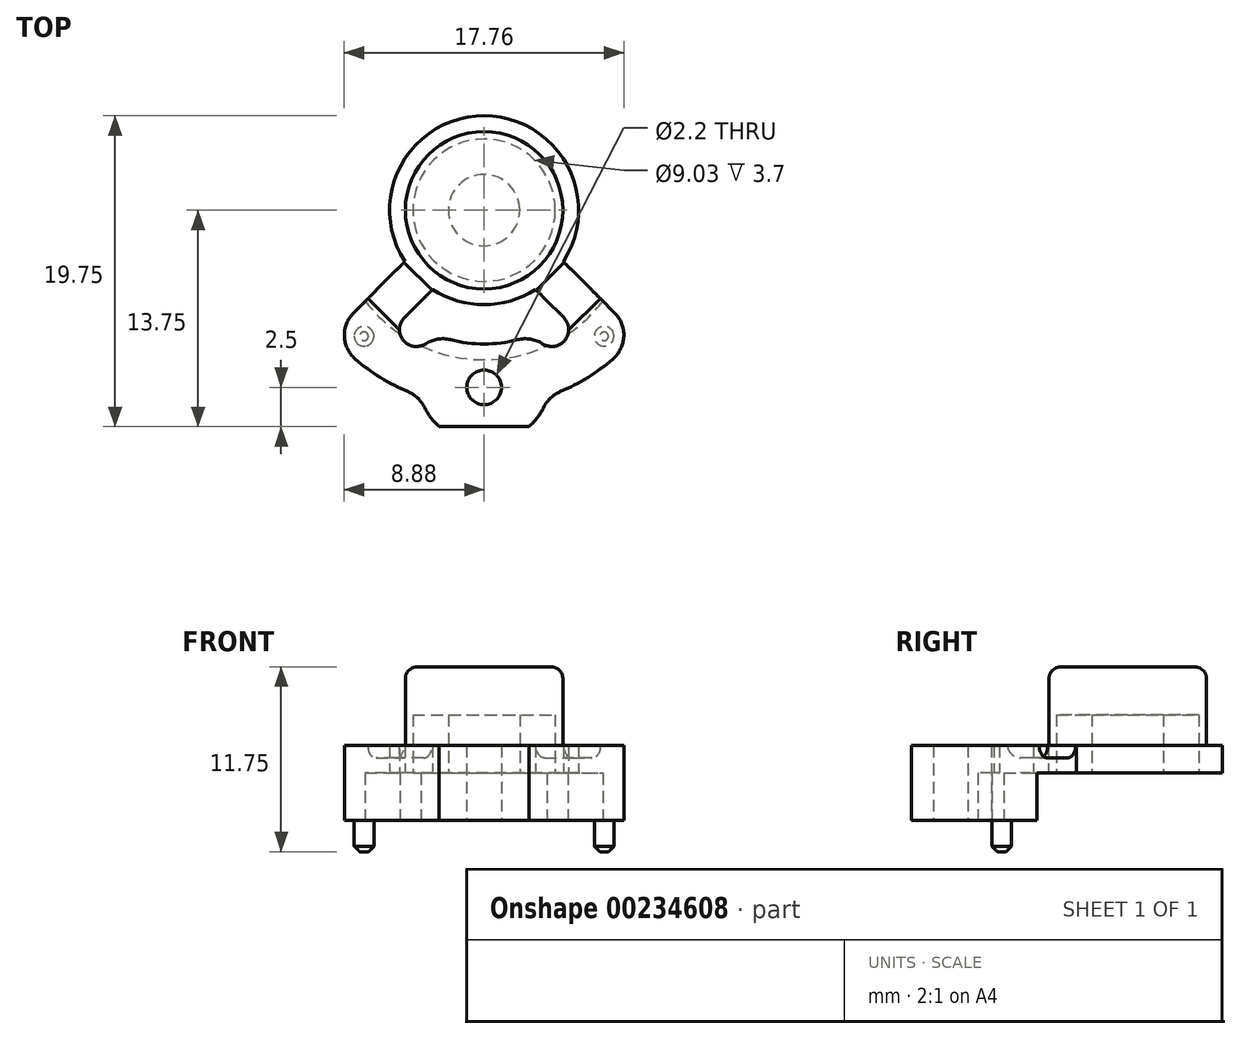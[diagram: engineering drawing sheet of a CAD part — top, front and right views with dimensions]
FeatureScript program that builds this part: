
annotation { "Feature Type Name" : "Feature", "Feature Type Description" : "" }
export const myFeature = defineFeature(function(context is Context, id is Id, definition is map)
    precondition{}
    {
        {
            var Q0;
            Q0=qCreatedBy(makeId("Top.planeOp"),FACE);
            var sketch = newSketch(context, id + "F0", { "sketchPlane" : qUnion([Q0])});
            skLineSegment(sketch, "E0.bottom", {"start": v(4, 3) * mm, "end": v(-4, 3) * mm, "construction": true});
            skLineSegment(sketch, "E0.top", {"start": v(4, -3) * mm, "end": v(-4, -3) * mm, "construction": true});
            skLineSegment(sketch, "E0.left", {"start": v(4, 3) * mm, "end": v(4, -3) * mm, "construction": true});
            skLineSegment(sketch, "E0.right", {"start": v(-4, 3) * mm, "end": v(-4, -3) * mm, "construction": true});
            skPoint(sketch, "E0.middle", {"position": v(0, 0) * mm});
            skArc(sketch, "E1", {"start": v(-9.68, -7.91) * mm, "mid": v(-7.15, -10.25) * mm, "end": v(-4.08, -11.82) * mm});
            skArc(sketch, "E2.converted", {"start": v(-3.27, -5.03) * mm, "mid": v(0, -6) * mm, "end": v(3.27, -5.03) * mm});
            skPoint(sketch, "E3.orphan", {"position": v(-6, 0) * mm});
            skLineSegment(sketch, "E4", {"start": v(0, 0) * mm, "end": v(14.62, -14.62) * mm, "construction": true});
            skLineSegment(sketch, "E5", {"start": v(5.03, -3.27) * mm, "end": v(9.68, -7.91) * mm});
            skLineSegment(sketch, "E6.MirrorCS", {"start": v(3.27, -5.03) * mm, "end": v(5.06, -6.83) * mm});
            skLineSegment(sketch, "E7.MirrorCS", {"start": v(-5.03, -3.27) * mm, "end": v(-9.68, -7.91) * mm});
            skLineSegment(sketch, "E8.MirrorCS", {"start": v(-3.27, -5.03) * mm, "end": v(-5.06, -6.83) * mm});
            skArc(sketch, "E9.MirrorCS", {"start": v(5.06, -6.83) * mm, "mid": v(4.83, -8.52) * mm, "end": v(3.27, -7.85) * mm});
            skArc(sketch, "E10.MirrorCS", {"start": v(-5.06, -6.83) * mm, "mid": v(-4.83, -8.52) * mm, "end": v(-3.27, -7.85) * mm});
            skArc(sketch, "E11.trimOffspring", {"start": v(-3.27, -7.85) * mm, "mid": v(0, -8.5) * mm, "end": v(3.27, -7.85) * mm});
            skArc(sketch, "E12.trimOffspring", {"start": v(5.03, -3.27) * mm, "mid": v(0, 6) * mm, "end": v(-5.03, -3.27) * mm});
            skArc(sketch, "E13.trimOffspring", {"start": v(4.08, -11.82) * mm, "mid": v(7.15, -10.25) * mm, "end": v(9.68, -7.91) * mm});
            skArc(sketch, "E14.trimOffspring", {"start": v(-4.08, -11.82) * mm, "mid": v(-3.6, -12.87) * mm, "end": v(-2.85, -13.75) * mm});
            skCircle(sketch, "E15", {"center": v(0, -11.25) * mm, "radius": 1.1 * mm});
            skPoint(sketch, "E16.orphan", {"position": v(-13.8, -3.13) * mm});
            skPoint(sketch, "E17.orphan", {"position": v(12.5, 0) * mm});
            skPoint(sketch, "E18.orphan", {"position": v(13.8, -3.13) * mm});
            skLineSegment(sketch, "E19", {"start": v(-2.85, -13.75) * mm, "end": v(2.85, -13.75) * mm});
            skArc(sketch, "E20.trimOffspring", {"start": v(2.85, -13.75) * mm, "mid": v(3.6, -12.87) * mm, "end": v(4.08, -11.82) * mm});
            skPoint(sketch, "E21.orphan", {"position": v(-6.83, -5.06) * mm});
            skPoint(sketch, "E22.start.orphan", {"position": v(-8.34, -1.67) * mm});
            skPoint(sketch, "E23.MirrorCS.end.orphan", {"position": v(-7.85, -3.27) * mm});
            skPoint(sketch, "E24.trimOffspring.end.orphan", {"position": v(8.34, -1.67) * mm});
            skPoint(sketch, "E25.end.orphan", {"position": v(7.85, -3.27) * mm});
            skPoint(sketch, "E25.start.orphan", {"position": v(6.83, -5.06) * mm});
            skSolve(sketch);
        }
        {
            var Q0;
            Q0=qSketchRegion(id+"F0",true);
            extrude(context, id + "F1", {"entities" : qUnion([Q0]), "depth" : 4.75 * mm});
        }
        {
            var Q0;
            Q0=makeQuery(id+"F1.opExtrude","CAP_FACE",FACE,{"disambiguationData":[OSD([sQuery(id+"F0.wireOp",EDGE,"E1"),sQuery(id+"F0.wireOp",EDGE,"E2.converted"),sQuery(id+"F0.wireOp",EDGE,"rdbc6vYB-NVjA-jXWY-TLaR-nZ7SSUkQD9Vy"),sQuery(id+"F0.wireOp",EDGE,"ynKpnGIP-DJsh-uGPF-F4s2-QlGlmaUKXdbb"),sQuery(id+"F0.wireOp",EDGE,"E22"),sQuery(id+"F0.wireOp",EDGE,"E5"),sQuery(id+"F0.wireOp",EDGE,"E6.MirrorCS"),sQuery(id+"F0.wireOp",EDGE,"E7.MirrorCS"),sQuery(id+"F0.wireOp",EDGE,"E8.MirrorCS"),sQuery(id+"F0.wireOp",EDGE,"E25"),sQuery(id+"F0.wireOp",EDGE,"E9.MirrorCS"),sQuery(id+"F0.wireOp",EDGE,"E24.trimOffspring"),sQuery(id+"F0.wireOp",EDGE,"E10.MirrorCS"),sQuery(id+"F0.wireOp",EDGE,"E23.MirrorCS"),sQuery(id+"F0.wireOp",EDGE,"E11.trimOffspring"),sQuery(id+"F0.wireOp",EDGE,"E12.trimOffspring")])],"isStart":false});
            var sketch = newSketch(context, id + "F2", { "sketchPlane" : qUnion([Q0])});
            skCircle(sketch, "E26", {"center": v(0, 0) * mm, "radius": 5 * mm});
            skSolve(sketch);
        }
        {
            var Q0;
            Q0=makeQuery(id+"F2.imprint","IMPRINT",FACE,{"disambiguationData":[TD([[makeQuery(id+"F2.imprint","IMPRINT",EDGE,{"derivedFrom":sQuery(id+"F2.wireOp",EDGE,"E26")}),1.0]])]});
            extrude(context, id + "F3", {"entities" : qUnion([Q0]), "operationType" : NewBodyOperationType.ADD, "depth" : 5 * mm});
        }
        {
            var Q0;
            Q0=makeQuery(id+"F1.opExtrude","CAP_FACE",FACE,{"disambiguationData":[OSD([sQuery(id+"F0.wireOp",EDGE,"E1"),sQuery(id+"F0.wireOp",EDGE,"E2.converted"),sQuery(id+"F0.wireOp",EDGE,"rdbc6vYB-NVjA-jXWY-TLaR-nZ7SSUkQD9Vy"),sQuery(id+"F0.wireOp",EDGE,"ynKpnGIP-DJsh-uGPF-F4s2-QlGlmaUKXdbb"),sQuery(id+"F0.wireOp",EDGE,"E22"),sQuery(id+"F0.wireOp",EDGE,"E5"),sQuery(id+"F0.wireOp",EDGE,"E6.MirrorCS"),sQuery(id+"F0.wireOp",EDGE,"E7.MirrorCS"),sQuery(id+"F0.wireOp",EDGE,"E8.MirrorCS"),sQuery(id+"F0.wireOp",EDGE,"E25"),sQuery(id+"F0.wireOp",EDGE,"E9.MirrorCS"),sQuery(id+"F0.wireOp",EDGE,"E24.trimOffspring"),sQuery(id+"F0.wireOp",EDGE,"E10.MirrorCS"),sQuery(id+"F0.wireOp",EDGE,"E23.MirrorCS"),sQuery(id+"F0.wireOp",EDGE,"E11.trimOffspring"),sQuery(id+"F0.wireOp",EDGE,"E12.trimOffspring")])],"isStart":false});
            var sketch = newSketch(context, id + "F4", { "sketchPlane" : qUnion([Q0])});
            skSolve(sketch);
        }
        {
            var Q0;
            Q0=makeQuery(id+"F1.opExtrude","SWEPT_EDGE",EDGE,{"disambiguationData":[OSD([sQuery(id+"F0.wireOp",EDGE,"E13.trimOffspring"),sQuery(id+"F0.wireOp",EDGE,"4655be30-1c85-40b4-9377-04363eb3a74c0.MirrorCS")])]});
            var Q1;
            Q1=makeQuery(id+"F1.opExtrude","SWEPT_EDGE",EDGE,{"disambiguationData":[OSD([sQuery(id+"F0.wireOp",EDGE,"E24.trimOffspring"),sQuery(id+"F0.wireOp",EDGE,"4655be30-1c85-40b4-9377-04363eb3a74c0.MirrorCS")])]});
            var Q2;
            Q2=makeQuery(id+"F1.opExtrude","SWEPT_EDGE",EDGE,{"disambiguationData":[OSD([sQuery(id+"F0.wireOp",EDGE,"E22"),sQuery(id+"F0.wireOp",EDGE,"H8J9w45X-FC2Y-JR27-rPcr-O6LJdDO2wVvT")])]});
            var Q3;
            Q3=makeQuery(id+"F1.opExtrude","SWEPT_EDGE",EDGE,{"disambiguationData":[OSD([sQuery(id+"F0.wireOp",EDGE,"E1"),sQuery(id+"F0.wireOp",EDGE,"H8J9w45X-FC2Y-JR27-rPcr-O6LJdDO2wVvT")])]});
            var Q4;
            Q4=makeQuery(id+"F1.opExtrude","SWEPT_EDGE",EDGE,{"disambiguationData":[OSD([sQuery(id+"F0.wireOp",EDGE,"E9.MirrorCS"),sQuery(id+"F0.wireOp",EDGE,"E11.trimOffspring")])]});
            var Q5;
            Q5=makeQuery(id+"F1.opExtrude","SWEPT_EDGE",EDGE,{"disambiguationData":[OSD([sQuery(id+"F0.wireOp",EDGE,"E10.MirrorCS"),sQuery(id+"F0.wireOp",EDGE,"E11.trimOffspring")])]});
            fillet(context, id + "F5", {"entities" : qUnion([Q0, Q1, Q2, Q3, Q4, Q5]), "radius" : 2 * mm, "tangentPropagation" : true, "allowEdgeOverflow" : false});
        }
        {
            var Q0;
            Q0=makeQuery(id+"F4.imprint","IMPRINT",FACE,{"disambiguationData":[TD([[makeQuery(id+"F4.imprint","IMPRINT",EDGE,{"derivedFrom":makeQuery(id+"F1.opExtrude","CAP_EDGE",EDGE,{"disambiguationData":[OSD([sQuery(id+"F0.wireOp",EDGE,"E1")])],"isStart":false})}),1.0]])]});
            var sketch = newSketch(context, id + "F6", { "sketchPlane" : qUnion([Q0])});
            skLineSegment(sketch, "E27", {"start": v(0, 0) * mm, "end": v(16.52, -16.52) * mm, "construction": true});
            skLineSegment(sketch, "E28", {"start": v(8.62, -4.38) * mm, "end": v(4.38, -8.62) * mm});
            skLineSegment(sketch, "E29", {"start": v(4.38, -8.62) * mm, "end": v(2.08, -6.32) * mm});
            skLineSegment(sketch, "E30", {"start": v(2.08, -6.32) * mm, "end": v(6.3, -2.1) * mm});
            skLineSegment(sketch, "E31", {"start": v(6.3, -2.1) * mm, "end": v(8.62, -4.38) * mm});
            skLineSegment(sketch, "E32.MirrorCS", {"start": v(-2.08, -6.32) * mm, "end": v(-6.3, -2.1) * mm});
            skLineSegment(sketch, "E33.MirrorCS", {"start": v(-6.3, -2.1) * mm, "end": v(-8.62, -4.38) * mm});
            skLineSegment(sketch, "E34.MirrorCS", {"start": v(-8.62, -4.38) * mm, "end": v(-4.38, -8.62) * mm});
            skLineSegment(sketch, "E35.MirrorCS", {"start": v(-4.38, -8.62) * mm, "end": v(-2.08, -6.32) * mm});
            skSolve(sketch);
        }
        {
            var Q0;
            Q0=qSketchRegion(id+"F6",true);
            extrude(context, id + "F7", {"entities" : qUnion([Q0]), "operationType" : NewBodyOperationType.REMOVE, "oppositeDirection" : true, "depth" : .8 * mm});
        }
        {
            var Q0;
            Q0=makeQuery(id+"F7.boolean.opBoolean","COPY",EDGE,{"derivedFrom":makeQuery(id+"F7.opExtrude","CAP_EDGE",EDGE,{"disambiguationData":[OSD([sQuery(id+"F6.wireOp",EDGE,"E30")])],"isStart":false})});
            var Q1;
            Q1=makeQuery(id+"F7.boolean.opBoolean","COPY",EDGE,{"derivedFrom":makeQuery(id+"F7.opExtrude","CAP_EDGE",EDGE,{"disambiguationData":[OSD([sQuery(id+"F6.wireOp",EDGE,"E32.MirrorCS")])],"isStart":false})});
            var Q2;
            Q2=makeQuery(id+"F3.opExtrude","CAP_EDGE",EDGE,{"disambiguationData":[OSD([sQuery(id+"F2.wireOp",EDGE,"E26")])],"isStart":true});
            var Q3;
            Q3=makeQuery(id+"F3.opExtrude","CAP_EDGE",EDGE,{"disambiguationData":[OSD([sQuery(id+"F2.wireOp",EDGE,"E26")])],"isStart":false});
            var Q4;
            Q4=makeQuery(id+"F7.boolean.opBoolean","COPY",EDGE,{"derivedFrom":makeQuery(id+"F7.opExtrude","CAP_EDGE",EDGE,{"disambiguationData":[OSD([sQuery(id+"F6.wireOp",EDGE,"E28")])],"isStart":false})});
            var Q5;
            Q5=makeQuery(id+"F7.boolean.opBoolean","COPY",EDGE,{"derivedFrom":makeQuery(id+"F7.opExtrude","CAP_EDGE",EDGE,{"disambiguationData":[OSD([sQuery(id+"F6.wireOp",EDGE,"E34.MirrorCS")])],"isStart":false})});
            fillet(context, id + "F8", {"entities" : qUnion([Q0, Q1, Q2, Q3, Q4, Q5]), "radius" : .75 * mm, "tangentPropagation" : true, "allowEdgeOverflow" : false});
        }
        {
            var Q0;
            Q0=qCreatedBy(makeId("Top.planeOp"),FACE);
            var sketch = newSketch(context, id + "F9", { "sketchPlane" : qUnion([Q0])});
            skCircle(sketch, "E36", {"center": v(0, 0) * mm, "radius": 9.5 * mm});
            skSolve(sketch);
        }
        {
            var Q0;
            Q0=qSketchRegion(id+"F9",true);
            extrude(context, id + "F10", {"entities" : qUnion([Q0]), "operationType" : NewBodyOperationType.REMOVE, "depth" : 3 * mm});
        }
        {
            var Q0;
            {var subQ0=sQuery(id+"F9.wireOp",EDGE,"E36");Q0=makeQuery(id+"F10.boolean.opBoolean","COPY",FACE,{"disambiguationData":[TD([makeQuery(id+"F1.opExtrude","SWEPT_FACE",FACE,{"disambiguationData":[OSD([sQuery(id+"F0.wireOp",EDGE,"E2.converted")])]})])],"derivedFrom":makeQuery(id+"F10.opExtrude","CAP_FACE",FACE,{"disambiguationData":[OSD([subQ0])],"isStart":false})});}
            var sketch = newSketch(context, id + "F11", { "sketchPlane" : qUnion([Q0])});
            skCircle(sketch, "E37", {"center": v(0, 0) * mm, "radius": 2 * mm});
            skSolve(sketch);
        }
        {
            var Q0;
            {var subQ0=sQuery(id+"F9.wireOp",EDGE,"E36");Q0=makeQuery(id+"F10.boolean.opBoolean","COPY",FACE,{"disambiguationData":[TD([makeQuery(id+"F1.opExtrude","SWEPT_FACE",FACE,{"disambiguationData":[OSD([sQuery(id+"F0.wireOp",EDGE,"E2.converted")])]})])],"derivedFrom":makeQuery(id+"F10.opExtrude","CAP_FACE",FACE,{"disambiguationData":[OSD([subQ0])],"isStart":false})});}
            var sketch = newSketch(context, id + "F12", { "sketchPlane" : qUnion([Q0])});
            skCircle(sketch, "E38", {"center": v(0, 0) * mm, "radius": 4.52 * mm});
            skCircle(sketch, "E39", {"center": v(0, 0) * mm, "radius": 2.27 * mm});
            skSolve(sketch);
        }
        {
            var Q0;
            Q0=qSketchRegion(id+"F12",true);
            extrude(context, id + "F13", {"entities" : qUnion([Q0]), "operationType" : NewBodyOperationType.REMOVE, "oppositeDirection" : true, "depth" : 3.7 * mm});
        }
        {
            var Q0;
            Q0=makeQuery(id+"F1.opExtrude","CAP_FACE",FACE,{"disambiguationData":[OSD([sQuery(id+"F0.wireOp",EDGE,"E1"),sQuery(id+"F0.wireOp",EDGE,"E2.converted"),sQuery(id+"F0.wireOp",EDGE,"E5"),sQuery(id+"F0.wireOp",EDGE,"E6.MirrorCS"),sQuery(id+"F0.wireOp",EDGE,"E7.MirrorCS"),sQuery(id+"F0.wireOp",EDGE,"E8.MirrorCS"),sQuery(id+"F0.wireOp",EDGE,"E9.MirrorCS"),sQuery(id+"F0.wireOp",EDGE,"E10.MirrorCS"),sQuery(id+"F0.wireOp",EDGE,"E11.trimOffspring"),sQuery(id+"F0.wireOp",EDGE,"E12.trimOffspring"),sQuery(id+"F0.wireOp",EDGE,"E13.trimOffspring"),sQuery(id+"F0.wireOp",EDGE,"E14.trimOffspring"),sQuery(id+"F0.wireOp",EDGE,"E15"),sQuery(id+"F0.wireOp",EDGE,"E19"),sQuery(id+"F0.wireOp",EDGE,"E20.trimOffspring")])],"isStart":true});
            var sketch = newSketch(context, id + "F14", { "sketchPlane" : qUnion([Q0])});
            skCircle(sketch, "E40", {"center": v(7.62, 8) * mm, "radius": 0.62 * mm});
            skPoint(sketch, "E40.centerSnap0", {"position": v(8.87, 8) * mm});
            skCircle(sketch, "E41.MirrorC", {"center": v(-7.62, 8) * mm, "radius": 0.62 * mm});
            skSolve(sketch);
        }
        {
            var Q0;
            Q0 = qSketchRegion(id + "F14", true);
            extrude(context, id + "F15", {"entities" : qUnion([Q0]), "operationType" : NewBodyOperationType.ADD, "depth" : 2 * mm});
        }
        {
            var Q0;
            Q0=makeQuery(id+"F15.opExtrude","CAP_EDGE",EDGE,{"disambiguationData":[OSD([sQuery(id+"F14.wireOp",EDGE,"E40")])],"isStart":false});
            var Q1;
            Q1=makeQuery(id+"F15.opExtrude","CAP_EDGE",EDGE,{"disambiguationData":[OSD([sQuery(id+"F14.wireOp",EDGE,"E41.MirrorC")])],"isStart":false});
            chamfer(context, id + "F16", {"entities" : qUnion([Q0, Q1]), "width" : .35 * mm, "tangentPropagation" : true});
        }
    });
